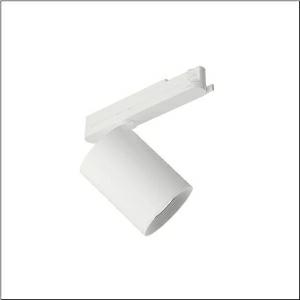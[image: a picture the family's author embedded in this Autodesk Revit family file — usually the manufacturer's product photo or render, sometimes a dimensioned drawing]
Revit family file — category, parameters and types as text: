
# Revit family: spot_11_51sd15mba5a
name_source: partatom
category: Lighting Fixtures
units: mm (PartAtom-declared; Revit-internal decimal feet)

## family parameters
Cut with Voids When Loaded = No
Host = Face
Light Source = No
Part Type = Normal
Room Calculation Point = No
Round Connector Dimension = Use Diameter
Shared = No

## types (1)
- --- (1 x LED, 7280 lm, 50.5 W, 2700K)
    Apparent Load = 51 VA
    CIE Flux Codes = 91 98 100 100 100
    Color Rendering = 90
    Color Temperature = 2700K
    Default Elevation = 1800 mm
    Description = Spot 11, directional spotlight, light control with lens, of PMMA, LED rated luminous flux: 5.680lm, light colour: 927, control gear: ECG Multilumen, with 3-phase adapter, mains connection: 220..240V, AC, 50/60Hz, of aluminium, traffic white (RAL 9016), length: 213mm, diameter: 105mm, protection rating (complete): IP20, insulation class (complete): insulation class I (protective earthing), certification: CE, impact resistance: IK02, permissible ambient temperature for indoor applications: -20..+40°C, packaging unit: 1 piece
    Height = 175 mm
    Lamp = 1 x LED
    Lamp Light Flux = 7280 lm
    Lamp Power = 50.5 W
    Lamp count = 1
    Length = 105 mm
    Luminous efficacy = 144 lm/W
    Manufacturer = Siteco
    ModVariant = No
    Model = 51SD15MBA5A
    Mounting Place = Ceiling
    Mounting Type = Pendant
    Number of Poles = 1
    OnlyDefault = Yes
    Power Factor = 1
    Product Name = Spot 11
    Product group = directional spotlight
    ProductGroupID = 906
    Protection Class = Protection class I
    Protection Degree = IP 20
    RLX_Detail_Level = 1
    RLX_Emergency_Light_Flux = 0 lm
    RLX_Emergency_Type = 0
    RLX_Emergency_Type_DB = No
    RlxData = <blob elided: 17729 chars, md5=9b326852>
    Socket = socket
    Standby Power = 0 W
    System Light Flux = 7280 lm
    System Power = 51 W
    Type Comments = factory setting: luminous flux: 100 % | (ON | ON | ON | ON) | 1050 mA
    Type Image = l_1006697.jpg
    URL = http://relux.com
    VarID = @adj_147002
    Voltage = 0 V
    Weight = 0.00 kg
    Width = 0 mm  [stored 0 ft]

note: [stored X ft] marks values corroborated as IEEE doubles in the binary element streams (Revit-internal decimal feet)

## geometry (parser evidence)
native form markers: Blend x4, Sweep x10
no freeform markers — native parametric forms only
